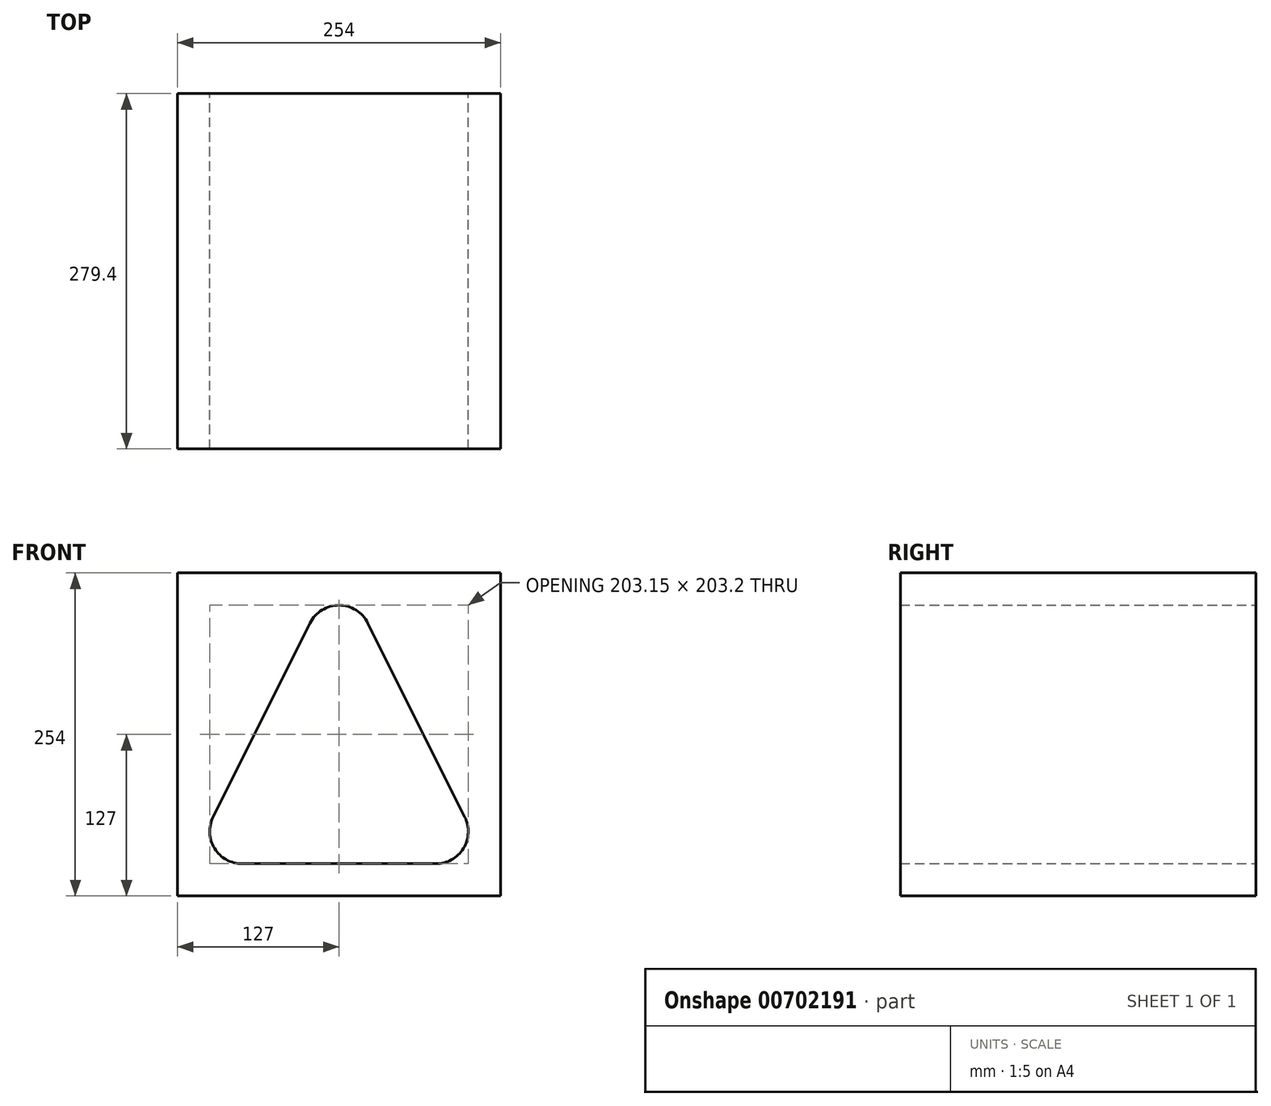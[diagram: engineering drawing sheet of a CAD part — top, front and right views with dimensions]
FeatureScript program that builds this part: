
annotation { "Feature Type Name" : "Feature", "Feature Type Description" : "" }
export const myFeature = defineFeature(function(context is Context, id is Id, definition is map)
    precondition{}
    {
        {
            var Q0;
            Q0=qCreatedBy(makeId("Front.planeOp"),FACE);
            var sketch = newSketch(context, id + "F0", { "sketchPlane" : qUnion([Q0])});
            skLineSegment(sketch, "E0", {"start": v(0, 0) * mm, "end": v(254, 0) * mm});
            skLineSegment(sketch, "E1", {"start": v(254, 0) * mm, "end": v(254, 254) * mm});
            skLineSegment(sketch, "E2", {"start": v(254, 254) * mm, "end": v(0, 254) * mm});
            skLineSegment(sketch, "E3", {"start": v(0, 254) * mm, "end": v(0, 0) * mm});
            skArc(sketch, "E4", {"start": v(28.08, 62.16) * mm, "mid": v(29.2, 37.45) * mm, "end": v(50.8, 25.4) * mm});
            skArc(sketch, "E5", {"start": v(203.2, 25.4) * mm, "mid": v(224.8, 37.45) * mm, "end": v(225.92, 62.16) * mm});
            skArc(sketch, "E6", {"start": v(149.72, 214.56) * mm, "mid": v(127, 228.6) * mm, "end": v(104.28, 214.56) * mm});
            skLineSegment(sketch, "E7", {"start": v(104.28, 214.56) * mm, "end": v(28.08, 62.16) * mm});
            skLineSegment(sketch, "E8", {"start": v(149.72, 214.56) * mm, "end": v(225.92, 62.16) * mm});
            skLineSegment(sketch, "E9", {"start": v(50.8, 25.4) * mm, "end": v(203.2, 25.4) * mm});
            skSolve(sketch);
        }
        {
            var Q0;
            Q0 = qSketchRegion(id + "F0", true);
            extrude(context, id + "F1", {"entities" : qUnion([Q0]), "depth" : 279.4 * mm, "offsetDistance" : 25.4 * mm});
        }
    });
